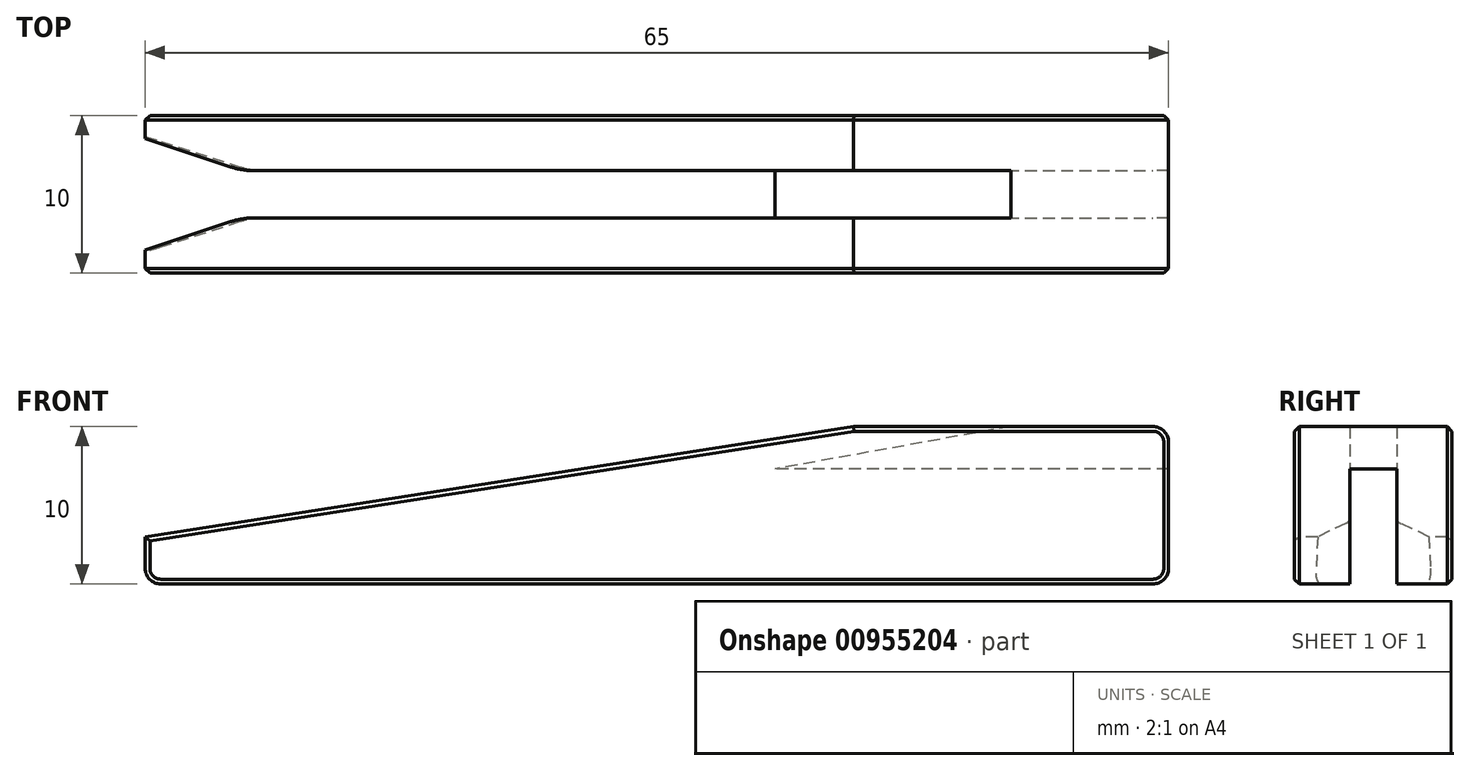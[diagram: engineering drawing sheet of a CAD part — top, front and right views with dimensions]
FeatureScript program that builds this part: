
annotation { "Feature Type Name" : "Feature", "Feature Type Description" : "" }
export const myFeature = defineFeature(function(context is Context, id is Id, definition is map)
    precondition{}
    {
        {
            var Q0;
            Q0=qCreatedBy(makeId("Top.planeOp"),FACE);
            var sketch = newSketch(context, id + "F0", { "sketchPlane" : qUnion([Q0])});
            skLineSegment(sketch, "E0", {"start": v(-79.64, 0) * mm, "end": v(46.17, 0) * mm, "construction": true});
            skLineSegment(sketch, "E1", {"start": v(-40, 1.5) * mm, "end": v(0, 1.5) * mm});
            skLineSegment(sketch, "E2", {"start": v(0, 1.5) * mm, "end": v(0, 0) * mm});
            skLineSegment(sketch, "E3", {"start": v(25, 0) * mm, "end": v(25, 5) * mm});
            skLineSegment(sketch, "E4", {"start": v(25, 5) * mm, "end": v(-40, 5) * mm});
            skLineSegment(sketch, "E5", {"start": v(-40, 5) * mm, "end": v(-40, 1.5) * mm});
            skLineSegment(sketch, "E6.MirrorCS", {"start": v(0, -1.5) * mm, "end": v(0, 0) * mm});
            skLineSegment(sketch, "E7.MirrorCS", {"start": v(25, 0) * mm, "end": v(25, -5) * mm});
            skLineSegment(sketch, "E8.MirrorCS", {"start": v(25, -5) * mm, "end": v(-40, -5) * mm});
            skLineSegment(sketch, "E9.MirrorCS", {"start": v(-40, -1.5) * mm, "end": v(0, -1.5) * mm});
            skLineSegment(sketch, "E10.MirrorCS", {"start": v(-40, -5) * mm, "end": v(-40, -1.5) * mm});
            skSolve(sketch);
        }
        {
            var Q0;
            Q0 = qSketchRegion(id + "F0", true);
            extrude(context, id + "F1", {"entities" : qUnion([Q0]), "depth" : 10 * mm, "offsetDistance" : 25 * mm});
        }
        {
            var Q0;
            Q0=makeQuery(id+"F1.opExtrude","SWEPT_FACE",FACE,{"disambiguationData":[OSD([sQuery(id+"F0.wireOp",EDGE,"E2"),sQuery(id+"F0.wireOp",EDGE,"E6.MirrorCS")])]});
            var sketch = newSketch(context, id + "F2", { "sketchPlane" : qUnion([Q0])});
            skLineSegment(sketch, "E11.bottom", {"start": v(-1.5, 0) * mm, "end": v(1.5, 0) * mm});
            skLineSegment(sketch, "E11.top", {"start": v(-1.5, 7.3) * mm, "end": v(1.5, 7.3) * mm});
            skLineSegment(sketch, "E11.left", {"start": v(-1.5, 0) * mm, "end": v(-1.5, 7.3) * mm});
            skLineSegment(sketch, "E11.right", {"start": v(1.5, 0) * mm, "end": v(1.5, 7.3) * mm});
            skSolve(sketch);
        }
        {
            var Q0;
            Q0 = qSketchRegion(id + "F2", true);
            extrude(context, id + "F3", {"entities" : qUnion([Q0]), "operationType" : NewBodyOperationType.REMOVE, "endBound" : BoundingType.THROUGH_ALL, "oppositeDirection" : true, "depth" : 25 * mm, "offsetDistance" : 25 * mm});
        }
        {
            var Q0;
            Q0=makeQuery(id+"F1.opExtrude","SWEPT_FACE",FACE,{"disambiguationData":[OSD([sQuery(id+"F0.wireOp",EDGE,"E8.MirrorCS")])]});
            var sketch = newSketch(context, id + "F4", { "sketchPlane" : qUnion([Q0])});
            skLineSegment(sketch, "E12", {"start": v(-40, 3) * mm, "end": v(5, 10) * mm});
            skLineSegment(sketch, "E13", {"start": v(5, 10) * mm, "end": v(-40, 10) * mm});
            skLineSegment(sketch, "E14", {"start": v(-40, 10) * mm, "end": v(-40, 3) * mm});
            skSolve(sketch);
        }
        {
            var Q0;
            Q0 = qSketchRegion(id + "F4", true);
            extrude(context, id + "F5", {"entities" : qUnion([Q0]), "operationType" : NewBodyOperationType.REMOVE, "endBound" : BoundingType.THROUGH_ALL, "oppositeDirection" : true, "depth" : 25 * mm, "offsetDistance" : 25 * mm});
        }
        {
            var Q0;
            {var subQ1=sQuery(id+"F0.wireOp",EDGE,"E8.MirrorCS");var subQ2=sQuery(id+"F0.wireOp",EDGE,"E7.MirrorCS");var subQ3=sQuery(id+"F0.wireOp",EDGE,"E3");Q0=makeQuery(id+"F3.boolean.opBoolean","SPLIT",EDGE,{"disambiguationData":[TD([makeQuery(id+"F1.opExtrude","SWEPT_FACE",FACE,{"disambiguationData":[OSD([subQ1])]})])],"derivedFrom":makeQuery(id+"F1.opExtrude","CAP_EDGE",EDGE,{"disambiguationData":[OSD([subQ3,subQ2])],"isStart":true})});}
            var Q1;
            {var subQ0=sQuery(id+"F0.wireOp",EDGE,"E7.MirrorCS");var subQ1=sQuery(id+"F0.wireOp",EDGE,"E3");var subQ3=sQuery(id+"F0.wireOp",EDGE,"E1");Q1=makeQuery(id+"F3.boolean.opBoolean","SPLIT",EDGE,{"disambiguationData":[TD([makeQuery(id+"F1.opExtrude","SWEPT_FACE",FACE,{"disambiguationData":[OSD([subQ3])]})])],"derivedFrom":makeQuery(id+"F1.opExtrude","CAP_EDGE",EDGE,{"disambiguationData":[OSD([subQ1,subQ0])],"isStart":true})});}
            var Q2;
            Q2=makeQuery(id+"F1.opExtrude","CAP_EDGE",EDGE,{"disambiguationData":[OSD([sQuery(id+"F0.wireOp",EDGE,"E10.MirrorCS")])],"isStart":true});
            var Q3;
            Q3=makeQuery(id+"F1.opExtrude","CAP_EDGE",EDGE,{"disambiguationData":[OSD([sQuery(id+"F0.wireOp",EDGE,"E5")])],"isStart":true});
            var Q4;
            {var subQ0=sQuery(id+"F0.wireOp",EDGE,"E10.MirrorCS");var subQ1=sQuery(id+"F4.wireOp",EDGE,"E12");Q4=makeQuery(id+"F5.boolean.opBoolean","COPY",EDGE,{"disambiguationData":[topologyDisambiguationEdgeConnected([makeQuery(id+"F1.opExtrude","SWEPT_FACE",FACE,{"disambiguationData":[OSD([subQ0])]})])],"derivedFrom":makeQuery(id+"F5.opExtrude","SWEPT_EDGE",EDGE,{"disambiguationData":[OSD([sQuery(id+"F0.wireOp",EDGE,"E8.MirrorCS"),subQ0,subQ1,sQuery(id+"F4.wireOp",EDGE,"E14")])]})});}
            var Q5;
            {var subQ0=sQuery(id+"F4.wireOp",EDGE,"E12");Q5=makeQuery(id+"F5.boolean.opBoolean","COPY",EDGE,{"disambiguationData":[topologyDisambiguationEdgeConnected([makeQuery(id+"F1.opExtrude","SWEPT_FACE",FACE,{"disambiguationData":[OSD([sQuery(id+"F0.wireOp",EDGE,"E5")])]})])],"derivedFrom":makeQuery(id+"F5.opExtrude","SWEPT_EDGE",EDGE,{"disambiguationData":[OSD([sQuery(id+"F0.wireOp",EDGE,"E8.MirrorCS"),sQuery(id+"F0.wireOp",EDGE,"E10.MirrorCS"),subQ0,sQuery(id+"F4.wireOp",EDGE,"E14")])]})});}
            var Q6;
            Q6=makeQuery(id+"F1.opExtrude","CAP_EDGE",EDGE,{"disambiguationData":[OSD([sQuery(id+"F0.wireOp",EDGE,"E3"),sQuery(id+"F0.wireOp",EDGE,"E7.MirrorCS")])],"isStart":false});
            fillet(context, id + "F6", {"entities" : qUnion([Q0, Q1, Q2, Q3, Q4, Q5, Q6]), "radius" : 1 * mm, "tangentPropagation" : true, "allowEdgeOverflow" : false});
        }
        {
            var Q0;
            Q0=qCreatedBy(makeId("Front.planeOp"),FACE);
            var sketch = newSketch(context, id + "F7", { "sketchPlane" : qUnion([Q0])});
            skLineSegment(sketch, "E15", {"start": v(0, 7.3) * mm, "end": v(0, 10) * mm});
            skLineSegment(sketch, "E16", {"start": v(0, 10) * mm, "end": v(15, 10) * mm});
            skLineSegment(sketch, "E17", {"start": v(15, 10) * mm, "end": v(0, 7.3) * mm});
            skSolve(sketch);
        }
        {
            var Q0;
            Q0 = qSketchRegion(id + "F7", true);
            extrude(context, id + "F8", {"entities" : qUnion([Q0]), "operationType" : NewBodyOperationType.REMOVE, "endBound" : BoundingType.SYMMETRIC, "depth" : 3 * mm, "offsetDistance" : 25 * mm});
        }
        {
            var Q0;
            {var subQ4=sQuery(id+"F0.wireOp",EDGE,"E1");var subQ5=sQuery(id+"F4.wireOp",EDGE,"E12");var subQ6=makeQuery(id+"F5.opExtrude","SWEPT_FACE",FACE,{"disambiguationData":[OSD([subQ5])]});Q0=makeQuery(id+"F8.boolean.opBoolean","SPLIT",FACE,{"disambiguationData":[TD([makeQuery(id+"F1.opExtrude","SWEPT_FACE",FACE,{"disambiguationData":[OSD([subQ4])]})])],"derivedFrom":makeQuery(id+"F5.boolean.opBoolean","COPY",FACE,{"derivedFrom":subQ6})});}
            var sketch = newSketch(context, id + "F9", { "sketchPlane" : qUnion([Q0])});
            skLineSegment(sketch, "E18", {"start": v(-46.22, 0) * mm, "end": v(30.93, 0) * mm, "construction": true});
            skLineSegment(sketch, "E19", {"start": v(-38.2, 3.25) * mm, "end": v(-28.2, 0) * mm});
            skLineSegment(sketch, "E20", {"start": v(-28.2, 0) * mm, "end": v(-38.2, -3.25) * mm});
            skLineSegment(sketch, "E21", {"start": v(-38.2, 3.25) * mm, "end": v(-47.18, 6.17) * mm});
            skLineSegment(sketch, "E22", {"start": v(-38.2, -3.25) * mm, "end": v(-46.71, -6.01) * mm});
            skLineSegment(sketch, "E23", {"start": v(-46.71, -6.01) * mm, "end": v(-47.18, 6.17) * mm});
            skSolve(sketch);
        }
        {
            var Q0;
            Q0 = qSketchRegion(id + "F9", true);
            extrude(context, id + "F10", {"entities" : qUnion([Q0]), "operationType" : NewBodyOperationType.REMOVE, "oppositeDirection" : true, "depth" : 25 * mm, "offsetDistance" : 25 * mm});
        }
        {
            var Q0;
            Q0=makeQuery(id+"F10.boolean.opBoolean","INTERSECT",EDGE,{"derivedFrom":[makeQuery(id+"F8.boolean.opBoolean","MERGE",FACE,{"derivedFrom":[makeQuery(id+"F3.boolean.opBoolean","MERGE",FACE,{"derivedFrom":[makeQuery(id+"F1.opExtrude","SWEPT_FACE",FACE,{"disambiguationData":[OSD([sQuery(id+"F0.wireOp",EDGE,"E1")])]})],"fromTools":[makeQuery(id+"F3.opExtrude","SWEPT_FACE",FACE,{"disambiguationData":[OSD([sQuery(id+"F2.wireOp",EDGE,"E11.left")])]})]})],"fromTools":[makeQuery(id+"F8.opExtrude","CAP_FACE",FACE,{"disambiguationData":[OSD([sQuery(id+"F7.wireOp",EDGE,"E15"),sQuery(id+"F7.wireOp",EDGE,"E16"),sQuery(id+"F7.wireOp",EDGE,"E17")])],"isStart":true})]}),makeQuery(id+"F10.opExtrude","SWEPT_FACE",FACE,{"disambiguationData":[OSD([sQuery(id+"F9.wireOp",EDGE,"E19"),sQuery(id+"F9.wireOp",EDGE,"E21")])]})]});
            var Q1;
            Q1=makeQuery(id+"F10.boolean.opBoolean","INTERSECT",EDGE,{"derivedFrom":[makeQuery(id+"F8.boolean.opBoolean","MERGE",FACE,{"derivedFrom":[makeQuery(id+"F3.boolean.opBoolean","MERGE",FACE,{"derivedFrom":[makeQuery(id+"F1.opExtrude","SWEPT_FACE",FACE,{"disambiguationData":[OSD([sQuery(id+"F0.wireOp",EDGE,"E9.MirrorCS")])]})],"fromTools":[makeQuery(id+"F3.opExtrude","SWEPT_FACE",FACE,{"disambiguationData":[OSD([sQuery(id+"F2.wireOp",EDGE,"E11.right")])]})]})],"fromTools":[makeQuery(id+"F8.opExtrude","CAP_FACE",FACE,{"disambiguationData":[OSD([sQuery(id+"F7.wireOp",EDGE,"E15"),sQuery(id+"F7.wireOp",EDGE,"E16"),sQuery(id+"F7.wireOp",EDGE,"E17")])],"isStart":false})]}),makeQuery(id+"F10.opExtrude","SWEPT_FACE",FACE,{"disambiguationData":[OSD([sQuery(id+"F9.wireOp",EDGE,"E20"),sQuery(id+"F9.wireOp",EDGE,"E22")])]})]});
            fillet(context, id + "F11", {"entities" : qUnion([Q0, Q1]), "radius" : 5 * mm, "tangentPropagation" : true, "allowEdgeOverflow" : false});
        }
        {
            var Q0;
            Q0=makeQuery(id+"F1.opExtrude","SWEPT_FACE",FACE,{"disambiguationData":[OSD([sQuery(id+"F0.wireOp",EDGE,"E4")])]});
            var Q1;
            Q1=makeQuery(id+"F1.opExtrude","SWEPT_FACE",FACE,{"disambiguationData":[OSD([sQuery(id+"F0.wireOp",EDGE,"E8.MirrorCS")])]});
            chamfer(context, id + "F12", {"entities" : qUnion([Q0, Q1]), "width" : 0.3 * mm, "tangentPropagation" : true});
        }
    });
